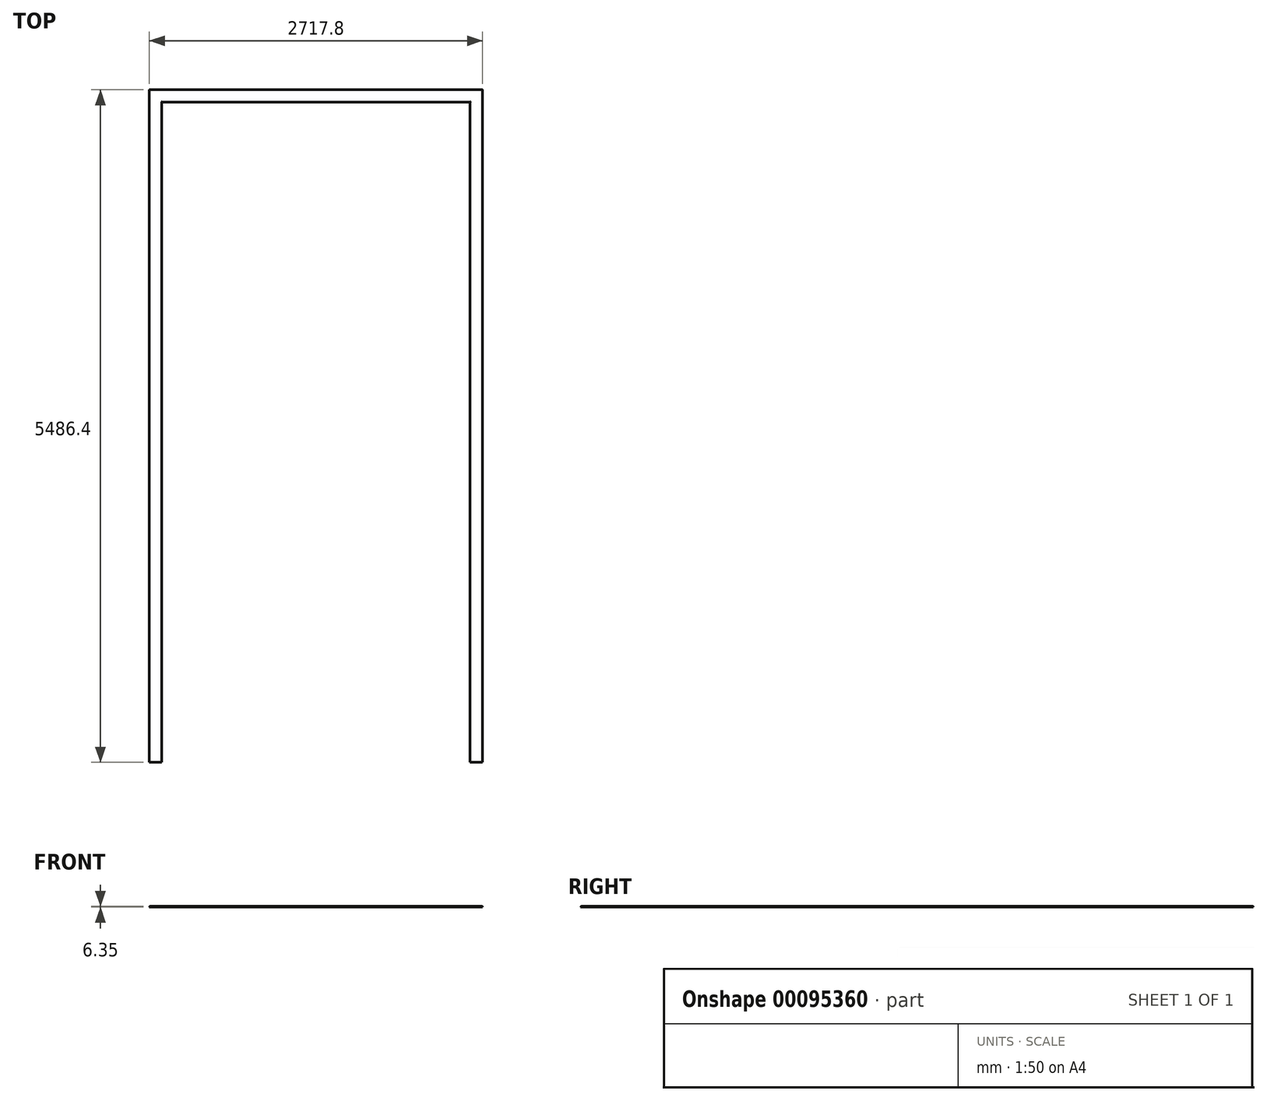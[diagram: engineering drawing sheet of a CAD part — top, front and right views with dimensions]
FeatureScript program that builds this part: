
annotation { "Feature Type Name" : "Feature", "Feature Type Description" : "" }
export const myFeature = defineFeature(function(context is Context, id is Id, definition is map)
    precondition{}
    {
        {
            var Q0;
            Q0=qCreatedBy(makeId("Top.planeOp"),FACE);
            var sketch = newSketch(context, id + "F0", { "sketchPlane" : qUnion([Q0])});
            skLineSegment(sketch, "E0.bottom", {"start": v(-1358.9, 2743.2) * mm, "end": v(-1257.3, 2743.2) * mm});
            skLineSegment(sketch, "E0.top", {"start": v(-1358.9, -2743.2) * mm, "end": v(-1257.3, -2743.2) * mm});
            skLineSegment(sketch, "E0.left", {"start": v(-1358.9, 2743.2) * mm, "end": v(-1358.9, -2743.2) * mm});
            skLineSegment(sketch, "E0.right", {"start": v(-1257.3, 2743.2) * mm, "end": v(-1257.3, -2743.2) * mm});
            skLineSegment(sketch, "E1.bottom", {"start": v(-1257.3, 2743.2) * mm, "end": v(1257.3, 2743.2) * mm});
            skLineSegment(sketch, "E1.top", {"start": v(-1257.3, 2641.6) * mm, "end": v(1257.3, 2641.6) * mm});
            skLineSegment(sketch, "E1.left", {"start": v(-1257.3, 2743.2) * mm, "end": v(-1257.3, 2641.6) * mm});
            skLineSegment(sketch, "E1.right", {"start": v(1257.3, 2743.2) * mm, "end": v(1257.3, 2641.6) * mm});
            skLineSegment(sketch, "E2.bottom", {"start": v(1257.3, 2743.2) * mm, "end": v(1358.9, 2743.2) * mm});
            skLineSegment(sketch, "E2.top", {"start": v(1257.3, -2743.2) * mm, "end": v(1358.9, -2743.2) * mm});
            skLineSegment(sketch, "E2.left", {"start": v(1257.3, 2743.2) * mm, "end": v(1257.3, -2743.2) * mm});
            skLineSegment(sketch, "E2.right", {"start": v(1358.9, 2743.2) * mm, "end": v(1358.9, -2743.2) * mm});
            skLineSegment(sketch, "E3", {"start": v(-1358.9, 2743.2) * mm, "end": v(1358.9, -2743.2) * mm, "construction": true});
            skLineSegment(sketch, "E4", {"start": v(-1358.9, -2743.2) * mm, "end": v(0, 0) * mm, "construction": true});
            skLineSegment(sketch, "E5", {"start": v(0, 0) * mm, "end": v(1358.9, 2743.2) * mm, "construction": true});
            skSolve(sketch);
        }
        {
            var Q0;
            Q0 = qSketchRegion(id + "F0", true);
            extrude(context, id + "F1", {"entities" : qUnion([Q0]), "depth" : 6.35 * mm});
        }
        {
            var Q0;
            Q0=makeQuery(id+"F1.opExtrude","CAP_EDGE",EDGE,{"disambiguationData":[OSD([sQuery(id+"F0.wireOp",EDGE,"E0.top")])],"isStart":false});
            var Q1;
            Q1=makeQuery(id+"F1.opExtrude","CAP_EDGE",EDGE,{"disambiguationData":[OSD([sQuery(id+"F0.wireOp",EDGE,"E0.left")])],"isStart":false});
            var Q2;
            Q2=makeQuery(id+"F1.opExtrude","CAP_EDGE",EDGE,{"disambiguationData":[OSD([sQuery(id+"F0.wireOp",EDGE,"E0.right")])],"isStart":false});
            var Q3;
            Q3=makeQuery(id+"F1.opExtrude","CAP_EDGE",EDGE,{"disambiguationData":[OSD([sQuery(id+"F0.wireOp",EDGE,"E1.top")])],"isStart":false});
            var Q4;
            Q4=makeQuery(id+"F1.opExtrude","CAP_EDGE",EDGE,{"disambiguationData":[OSD([sQuery(id+"F0.wireOp",EDGE,"E0.bottom"),sQuery(id+"F0.wireOp",EDGE,"E1.bottom"),sQuery(id+"F0.wireOp",EDGE,"E2.bottom")])],"isStart":false});
            var Q5;
            Q5=makeQuery(id+"F1.opExtrude","CAP_EDGE",EDGE,{"disambiguationData":[OSD([sQuery(id+"F0.wireOp",EDGE,"E2.right")])],"isStart":false});
            var Q6;
            Q6=makeQuery(id+"F1.opExtrude","CAP_EDGE",EDGE,{"disambiguationData":[OSD([sQuery(id+"F0.wireOp",EDGE,"E2.left")])],"isStart":false});
            var Q7;
            Q7=makeQuery(id+"F1.opExtrude","CAP_EDGE",EDGE,{"disambiguationData":[OSD([sQuery(id+"F0.wireOp",EDGE,"E2.top")])],"isStart":false});
            fillet(context, id + "F2", {"entities" : qUnion([Q0, Q1, Q2, Q3, Q4, Q5, Q6, Q7]), "radius" : 5.08 * mm, "tangentPropagation" : true, "allowEdgeOverflow" : false});
        }
    });
